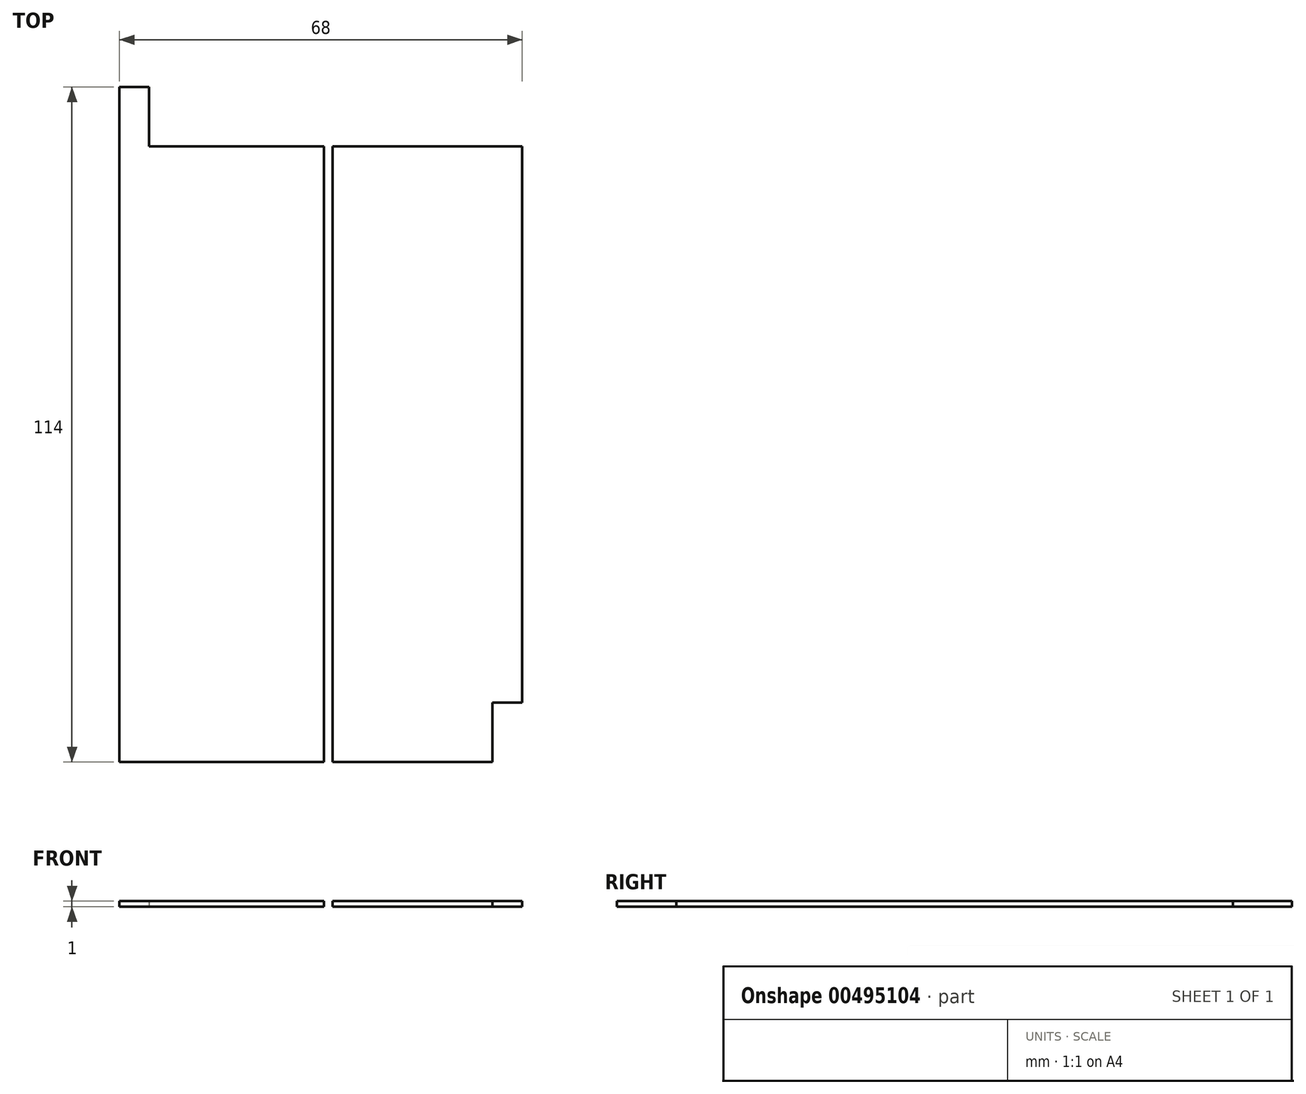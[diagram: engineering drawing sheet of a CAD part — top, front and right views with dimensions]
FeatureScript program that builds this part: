
annotation { "Feature Type Name" : "Feature", "Feature Type Description" : "" }
export const myFeature = defineFeature(function(context is Context, id is Id, definition is map)
    precondition{}
    {
        {
            var Q0;
            Q0=qCreatedBy(makeId("Top.planeOp"),FACE);
            var sketch = newSketch(context, id + "F0", { "sketchPlane" : qUnion([Q0])});
            skLineSegment(sketch, "E0.bottom", {"start": v(-34, 52) * mm, "end": v(34, 52) * mm});
            skLineSegment(sketch, "E0.top", {"start": v(-34, -52) * mm, "end": v(34, -52) * mm});
            skLineSegment(sketch, "E0.left", {"start": v(-34, 52) * mm, "end": v(-34, -52) * mm});
            skLineSegment(sketch, "E0.right", {"start": v(34, 52) * mm, "end": v(34, -52) * mm});
            skPoint(sketch, "E0.middle", {"position": v(0, 0) * mm});
            skLineSegment(sketch, "E1", {"start": v(0, 52) * mm, "end": v(0, -52) * mm});
            skLineSegment(sketch, "E2", {"start": v(0, -52) * mm, "end": v(0.5, -52) * mm});
            skLineSegment(sketch, "E3", {"start": v(0.5, -52) * mm, "end": v(-0.5, -52) * mm});
            skLineSegment(sketch, "E4", {"start": v(-0.5, -52) * mm, "end": v(-0.5, 52) * mm});
            skLineSegment(sketch, "E5", {"start": v(-0.5, 52) * mm, "end": v(0.5, 52) * mm});
            skLineSegment(sketch, "E6", {"start": v(0.5, 52) * mm, "end": v(-0.5, 52) * mm});
            skLineSegment(sketch, "E7", {"start": v(0.5, 52) * mm, "end": v(0.5, -52) * mm});
            skLineSegment(sketch, "E8.bottom", {"start": v(-34, 52) * mm, "end": v(-29, 52) * mm});
            skLineSegment(sketch, "E8.top", {"start": v(-34, 62) * mm, "end": v(-29, 62) * mm});
            skLineSegment(sketch, "E8.left", {"start": v(-34, 52) * mm, "end": v(-34, 62) * mm});
            skLineSegment(sketch, "E8.right", {"start": v(-29, 52) * mm, "end": v(-29, 62) * mm});
            skSolve(sketch);
        }
        {
            var Q0;
            Q0 = qSketchRegion(id + "F0", true);
            extrude(context, id + "F1", {"entities" : qUnion([Q0]), "depth" : 1 * mm});
        }
        {
            var Q0;
            Q0=makeQuery(id+"F1.opExtrude","CAP_FACE",FACE,{"disambiguationData":[OSD([sQuery(id+"F0.wireOp",EDGE,"E0.bottom"),sQuery(id+"F0.wireOp",EDGE,"E0.top"),sQuery(id+"F0.wireOp",EDGE,"E0.left"),sQuery(id+"F0.wireOp",EDGE,"E0.right"),sQuery(id+"F0.wireOp",EDGE,"E3"),sQuery(id+"F0.wireOp",EDGE,"E6")])],"isStart":false});
            var sketch = newSketch(context, id + "F2", { "sketchPlane" : qUnion([Q0])});
            skPoint(sketch, "E9", {"position": v(2.5, 52) * mm});
            skPoint(sketch, "E10", {"position": v(2, 52) * mm});
            skPoint(sketch, "E11", {"position": v(0, -52) * mm});
            skPoint(sketch, "E12", {"position": v(0.5, -52) * mm});
            skPoint(sketch, "E13", {"position": v(-0.5, -52) * mm});
            skLineSegment(sketch, "E14.bottom", {"start": v(0.5, 52) * mm, "end": v(2, 52) * mm});
            skLineSegment(sketch, "E14.top", {"start": v(0.5, -52) * mm, "end": v(2, -52) * mm});
            skLineSegment(sketch, "E14.left", {"start": v(2, 52) * mm, "end": v(2, -52) * mm});
            skLineSegment(sketch, "E14.right", {"start": v(0.5, 52) * mm, "end": v(0.5, -52) * mm});
            skSolve(sketch);
        }
        {
            var Q0;
            Q0 = qSketchRegion(id + "F2", true);
            extrude(context, id + "F3", {"entities" : qUnion([Q0]), "operationType" : NewBodyOperationType.REMOVE, "oppositeDirection" : true, "depth" : 1 * mm});
        }
        {
            var Q0;
            {var subQ0=sQuery(id+"F0.wireOp",EDGE,"E6");var subQ1=sQuery(id+"F0.wireOp",EDGE,"E0.bottom");var subQ2=sQuery(id+"F0.wireOp",EDGE,"E3");var subQ3=sQuery(id+"F0.wireOp",EDGE,"E0.top");var subQ4=sQuery(id+"F0.wireOp",EDGE,"E0.right");Q0=makeQuery(id+"F3.boolean.opBoolean","SPLIT",FACE,{"disambiguationData":[TD([makeQuery(id+"F1.opExtrude","SWEPT_FACE",FACE,{"disambiguationData":[OSD([subQ4])]})])],"derivedFrom":makeQuery(id+"F1.opExtrude","CAP_FACE",FACE,{"disambiguationData":[OSD([subQ1,subQ3,sQuery(id+"F0.wireOp",EDGE,"E0.left"),subQ4,subQ2,subQ0])],"isStart":false})});}
            var sketch = newSketch(context, id + "F4", { "sketchPlane" : qUnion([Q0])});
            skLineSegment(sketch, "E15.bottom", {"start": v(34, -52) * mm, "end": v(29, -52) * mm});
            skLineSegment(sketch, "E15.top", {"start": v(34, -42) * mm, "end": v(29, -42) * mm});
            skLineSegment(sketch, "E15.left", {"start": v(34, -52) * mm, "end": v(34, -42) * mm});
            skLineSegment(sketch, "E15.right", {"start": v(29, -52) * mm, "end": v(29, -42) * mm});
            skSolve(sketch);
        }
        {
            var Q0;
            Q0 = qSketchRegion(id + "F4", true);
            extrude(context, id + "F5", {"entities" : qUnion([Q0]), "operationType" : NewBodyOperationType.REMOVE, "oppositeDirection" : true, "depth" : 1 * mm});
        }
    });
